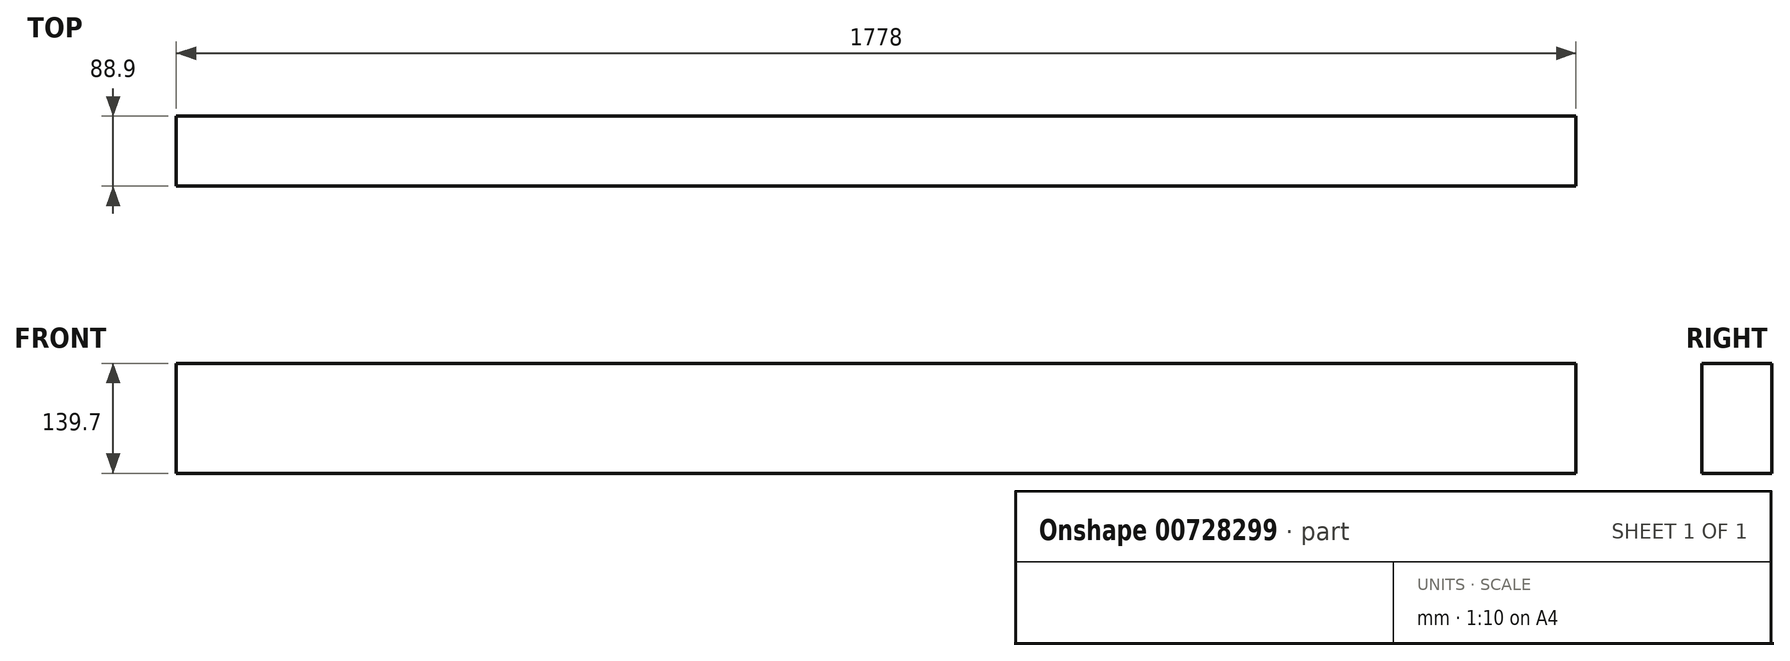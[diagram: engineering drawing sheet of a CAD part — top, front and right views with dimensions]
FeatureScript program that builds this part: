
annotation { "Feature Type Name" : "Feature", "Feature Type Description" : "" }
export const myFeature = defineFeature(function(context is Context, id is Id, definition is map)
    precondition{}
    {
        {
            var Q0;
            Q0=qCreatedBy(makeId("Front.planeOp"),FACE);
            var sketch = newSketch(context, id + "F0", { "sketchPlane" : qUnion([Q0])});
            skLineSegment(sketch, "E0.bottom", {"start": v(-889, -69.85) * mm, "end": v(889, -69.85) * mm});
            skLineSegment(sketch, "E0.top", {"start": v(-889, 69.85) * mm, "end": v(889, 69.85) * mm});
            skLineSegment(sketch, "E0.left", {"start": v(-889, -69.85) * mm, "end": v(-889, 69.85) * mm});
            skLineSegment(sketch, "E0.right", {"start": v(889, -69.85) * mm, "end": v(889, 69.85) * mm});
            skPoint(sketch, "E0.middle", {"position": v(0, 0) * mm});
            skSolve(sketch);
        }
        {
            var Q0;
            Q0=qSketchRegion(id+"F0",true);
            extrude(context, id + "F1", {"entities" : qUnion([Q0]), "depth" : 88.9 * mm, "offsetDistance" : 25.4 * mm});
        }
    });
